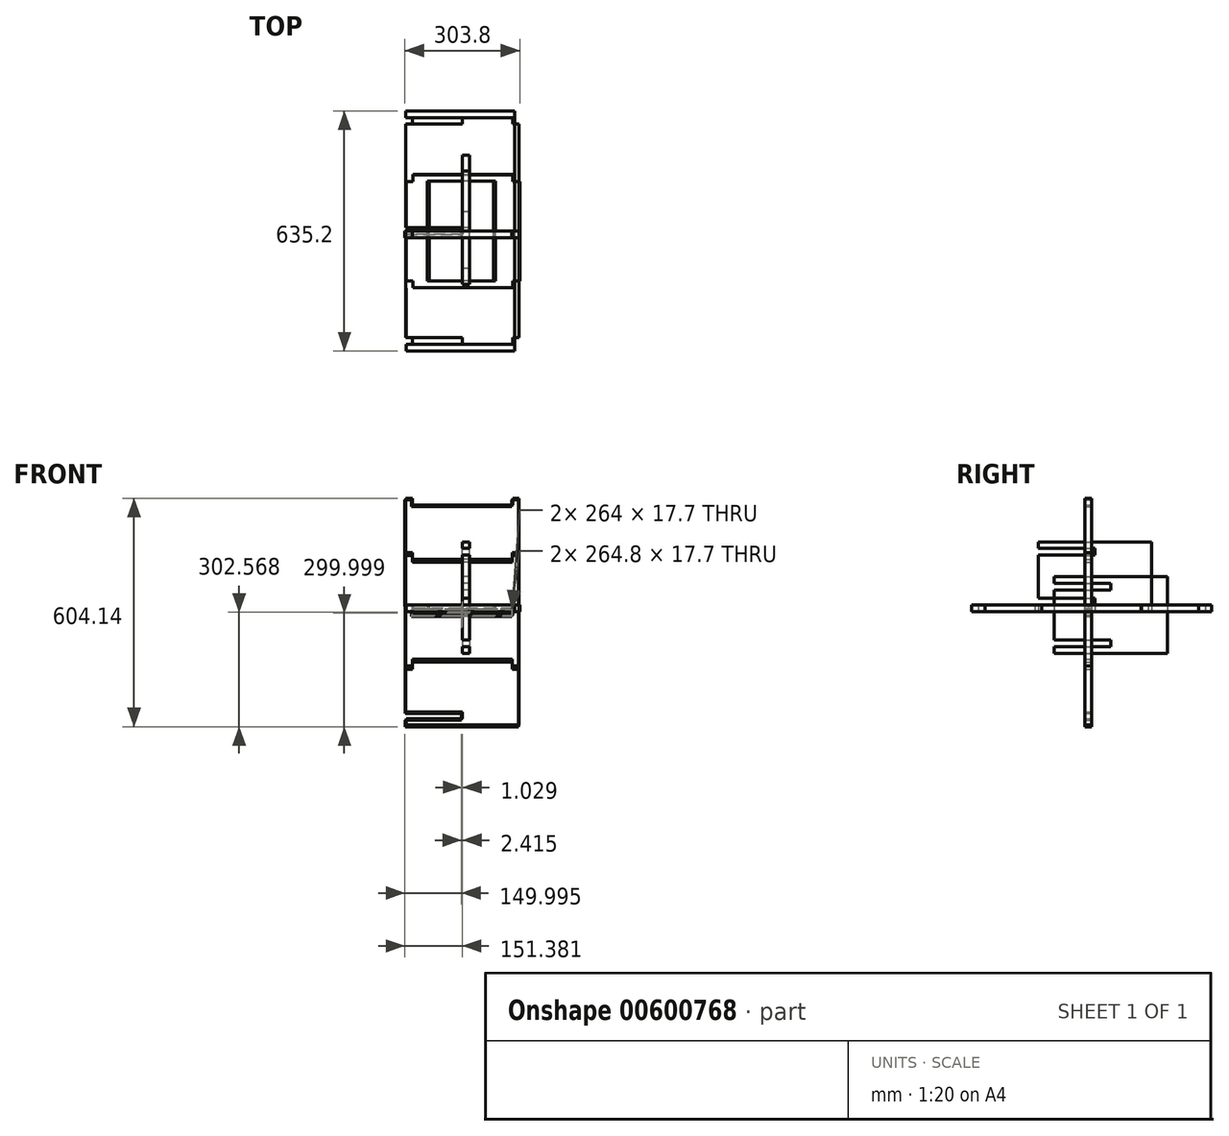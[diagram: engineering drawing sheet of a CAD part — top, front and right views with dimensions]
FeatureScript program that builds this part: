
annotation { "Feature Type Name" : "Feature", "Feature Type Description" : "" }
export const myFeature = defineFeature(function(context is Context, id is Id, definition is map)
    precondition{}
    {
        {
            var Q0;
            Q0=qCreatedBy(makeId("Front.planeOp"),FACE);
            var sketch = newSketch(context, id + "F0", { "sketchPlane" : qUnion([Q0])});
            skLineSegment(sketch, "E0.left", {"start": v(150, -300) * mm, "end": v(150, 300) * mm});
            skLineSegment(sketch, "E1", {"start": v(-150, 300) * mm, "end": v(-132.4, 300) * mm});
            skLineSegment(sketch, "E2", {"start": v(-132.4, 300) * mm, "end": v(-132.4, 282.4) * mm});
            skLineSegment(sketch, "E3", {"start": v(150, 300) * mm, "end": v(132.4, 300) * mm});
            skLineSegment(sketch, "E4", {"start": v(132.4, 300) * mm, "end": v(132.4, 282.4) * mm});
            skLineSegment(sketch, "E5", {"start": v(132.4, 282.4) * mm, "end": v(-132.4, 282.4) * mm});
            skLineSegment(sketch, "E6", {"start": v(150, -300) * mm, "end": v(-149.6, -300) * mm});
            skLineSegment(sketch, "E7", {"start": v(-149.6, -300) * mm, "end": v(-149.6, -282.4) * mm});
            skLineSegment(sketch, "E8", {"start": v(-149.6, -282.4) * mm, "end": v(0, -282.4) * mm});
            skLineSegment(sketch, "E9", {"start": v(0, -282.4) * mm, "end": v(0, -264.8) * mm});
            skLineSegment(sketch, "E10", {"start": v(0, -264.8) * mm, "end": v(-149.73, -264.8) * mm});
            skLineSegment(sketch, "E11", {"start": v(-149.73, -264.8) * mm, "end": v(-150, 300) * mm});
            skLineSegment(sketch, "E12.bottom", {"start": v(132.4, -8.85) * mm, "end": v(-132.4, -8.85) * mm});
            skLineSegment(sketch, "E12.top", {"start": v(132.4, 8.85) * mm, "end": v(-132.4, 8.85) * mm});
            skLineSegment(sketch, "E12.left", {"start": v(132.4, -8.85) * mm, "end": v(132.4, 8.85) * mm});
            skLineSegment(sketch, "E12.right", {"start": v(-132.4, -8.85) * mm, "end": v(-132.4, 8.85) * mm});
            skPoint(sketch, "E12.middle", {"position": v(0, 0) * mm});
            skSolve(sketch);
        }
        {
            var Q0;
            Q0=qCreatedBy(makeId("Front.planeOp"),FACE);
            var sketch = newSketch(context, id + "F1", { "sketchPlane" : qUnion([Q0])});
            skLineSegment(sketch, "E13.left", {"start": v(147.59, -304.14) * mm, "end": v(147.59, 295.86) * mm});
            skLineSegment(sketch, "E14", {"start": v(-152.41, 295.86) * mm, "end": v(-134.81, 295.86) * mm});
            skLineSegment(sketch, "E15", {"start": v(-134.81, 295.86) * mm, "end": v(-134.81, 278.26) * mm});
            skLineSegment(sketch, "E16", {"start": v(147.59, 295.86) * mm, "end": v(129.99, 295.86) * mm});
            skLineSegment(sketch, "E17", {"start": v(129.99, 295.86) * mm, "end": v(129.99, 278.26) * mm});
            skLineSegment(sketch, "E18", {"start": v(129.99, 278.26) * mm, "end": v(-134.81, 278.26) * mm});
            skLineSegment(sketch, "E19", {"start": v(147.59, -304.14) * mm, "end": v(-152.02, -304.14) * mm});
            skLineSegment(sketch, "E20", {"start": v(-152.02, -304.14) * mm, "end": v(-152.02, -286.54) * mm});
            skLineSegment(sketch, "E21", {"start": v(-152.02, -286.54) * mm, "end": v(-2.41, -286.54) * mm});
            skLineSegment(sketch, "E22", {"start": v(-2.41, -286.54) * mm, "end": v(-2.41, -268.94) * mm});
            skLineSegment(sketch, "E23", {"start": v(-2.41, -268.94) * mm, "end": v(-152.15, -268.94) * mm});
            skLineSegment(sketch, "E24", {"start": v(-152.15, -268.94) * mm, "end": v(-152.41, 295.86) * mm});
            skLineSegment(sketch, "E25.bottom", {"start": v(129.99, -13) * mm, "end": v(-134.81, -13) * mm});
            skLineSegment(sketch, "E25.top", {"start": v(129.99, 4.7) * mm, "end": v(-134.81, 4.7) * mm});
            skLineSegment(sketch, "E25.left", {"start": v(129.99, -13) * mm, "end": v(129.99, 4.7) * mm});
            skLineSegment(sketch, "E25.right", {"start": v(-134.81, -13) * mm, "end": v(-134.81, 4.7) * mm});
            skPoint(sketch, "E25.middle", {"position": v(-2.41, -4.14) * mm});
            skSolve(sketch);
        }
        {
            var Q0;
            Q0=qCreatedBy(makeId("Top.planeOp"),FACE);
            var sketch = newSketch(context, id + "F2", { "sketchPlane" : qUnion([Q0])});
            skLineSegment(sketch, "E26.left", {"start": v(149.99, -282.54) * mm, "end": v(149.99, 282.26) * mm});
            skLineSegment(sketch, "E27", {"start": v(-132.41, 299.86) * mm, "end": v(-132.41, 282.26) * mm});
            skLineSegment(sketch, "E28", {"start": v(132.39, 299.86) * mm, "end": v(132.39, 282.26) * mm});
            skLineSegment(sketch, "E29.bottom", {"start": v(0, -9) * mm, "end": v(-132.41, -9) * mm});
            skLineSegment(sketch, "E29.top", {"start": v(0, 8.7) * mm, "end": v(-132.41, 8.7) * mm});
            skPoint(sketch, "E29.middle", {"position": v(-0.01, -0.14) * mm});
            skLineSegment(sketch, "E30", {"start": v(132.39, -300.14) * mm, "end": v(132.39, -282.54) * mm});
            skLineSegment(sketch, "E31", {"start": v(-132.41, -300.14) * mm, "end": v(-132.41, -282.54) * mm});
            skLineSegment(sketch, "E32", {"start": v(-150.01, 282.26) * mm, "end": v(-150.01, 8.7) * mm});
            skLineSegment(sketch, "E33", {"start": v(-132.41, -282.54) * mm, "end": v(-150.01, -282.54) * mm});
            skLineSegment(sketch, "E34", {"start": v(132.39, -282.54) * mm, "end": v(149.99, -282.54) * mm});
            skLineSegment(sketch, "E35", {"start": v(-132.41, -300.14) * mm, "end": v(132.39, -300.14) * mm});
            skLineSegment(sketch, "E36", {"start": v(-132.41, 282.26) * mm, "end": v(-150.01, 282.26) * mm});
            skLineSegment(sketch, "E37", {"start": v(132.39, 282.26) * mm, "end": v(149.99, 282.26) * mm});
            skLineSegment(sketch, "E38", {"start": v(-132.41, 299.86) * mm, "end": v(132.39, 299.86) * mm});
            skLineSegment(sketch, "E39", {"start": v(0, 8.7) * mm, "end": v(0, -9) * mm});
            skLineSegment(sketch, "E40", {"start": v(-132.41, 8.7) * mm, "end": v(-150.01, 8.7) * mm});
            skLineSegment(sketch, "E41", {"start": v(-132.41, -9) * mm, "end": v(-150.01, -9) * mm});
            skLineSegment(sketch, "E42.trimOffspring", {"start": v(-150.01, -9) * mm, "end": v(-150.01, -282.54) * mm});
            skSolve(sketch);
        }
        {
            var Q0;
            Q0=qCreatedBy(makeId("Top.planeOp"),FACE);
            var sketch = newSketch(context, id + "F3", { "sketchPlane" : qUnion([Q0])});
            skLineSegment(sketch, "E43", {"start": v(-149.73, 8.71) * mm, "end": v(0.13, 8.71) * mm});
            skLineSegment(sketch, "E44", {"start": v(-149.73, -9) * mm, "end": v(0, -8.99) * mm});
            skLineSegment(sketch, "E45", {"start": v(0.13, 8.71) * mm, "end": v(0, -8.99) * mm});
            skLineSegment(sketch, "E46", {"start": v(-149.87, 299.86) * mm, "end": v(0, 299.86) * mm});
            skLineSegment(sketch, "E47", {"start": v(-149.48, -300.14) * mm, "end": v(0, -300.14) * mm});
            skLineSegment(sketch, "E48", {"start": v(-149.48, -300.14) * mm, "end": v(-149.48, -317.74) * mm});
            skLineSegment(sketch, "E49", {"start": v(-149.48, -317.74) * mm, "end": v(137.6, -317.74) * mm});
            skLineSegment(sketch, "E50", {"start": v(0, -282.54) * mm, "end": v(0, -300.14) * mm});
            skLineSegment(sketch, "E51", {"start": v(0, -282.54) * mm, "end": v(-149.48, -282.54) * mm});
            skLineSegment(sketch, "E52", {"start": v(-149.73, -9) * mm, "end": v(-149.48, -282.54) * mm});
            skLineSegment(sketch, "E53", {"start": v(137.6, 299.86) * mm, "end": v(137.6, -317.74) * mm});
            skLineSegment(sketch, "E54", {"start": v(-149.86, 282.26) * mm, "end": v(0, 282.33) * mm});
            skLineSegment(sketch, "E55", {"start": v(-149.87, 299.86) * mm, "end": v(-149.87, 317.46) * mm});
            skLineSegment(sketch, "E56", {"start": v(-149.87, 317.46) * mm, "end": v(137.6, 317.46) * mm});
            skLineSegment(sketch, "E57", {"start": v(137.6, 299.86) * mm, "end": v(137.6, 317.46) * mm});
            skLineSegment(sketch, "E58", {"start": v(0, 282.33) * mm, "end": v(0, 299.86) * mm});
            skLineSegment(sketch, "E59", {"start": v(-149.86, 282.26) * mm, "end": v(-149.73, 8.71) * mm});
            skSolve(sketch);
        }
        {
            var Q0;
            Q0=qCreatedBy(makeId("Top.planeOp"),FACE);
            var sketch = newSketch(context, id + "F4", { "sketchPlane" : qUnion([Q0])});
            skLineSegment(sketch, "E60.bottom", {"start": v(133.13, -150.22) * mm, "end": v(-131.67, -150.22) * mm});
            skPoint(sketch, "E60.middle", {"position": v(0.33, -0.22) * mm});
            skLineSegment(sketch, "E61.left", {"start": v(133.13, 130.98) * mm, "end": v(133.13, 148.98) * mm});
            skLineSegment(sketch, "E61.right", {"start": v(-131.67, 130.98) * mm, "end": v(-131.67, 148.98) * mm});
            skLineSegment(sketch, "E62.left", {"start": v(133.13, -132.22) * mm, "end": v(133.13, -150.22) * mm});
            skLineSegment(sketch, "E62.right", {"start": v(-131.67, -132.22) * mm, "end": v(-131.67, -150.22) * mm});
            skLineSegment(sketch, "E63", {"start": v(-131.67, 148.98) * mm, "end": v(133.13, 148.98) * mm});
            skLineSegment(sketch, "E64", {"start": v(-131.67, 130.98) * mm, "end": v(-149.67, 130.98) * mm});
            skLineSegment(sketch, "E65", {"start": v(133.13, 130.98) * mm, "end": v(151.13, 130.98) * mm});
            skLineSegment(sketch, "E66", {"start": v(-131.67, -132.22) * mm, "end": v(-149.67, -132.22) * mm});
            skLineSegment(sketch, "E67", {"start": v(133.13, -132.22) * mm, "end": v(151.13, -132.22) * mm});
            skLineSegment(sketch, "E68", {"start": v(0.33, 8.38) * mm, "end": v(0.33, -9.22) * mm});
            skLineSegment(sketch, "E69.trimOffspring", {"start": v(-149.67, 8.38) * mm, "end": v(-149.67, 130.98) * mm});
            skLineSegment(sketch, "E70", {"start": v(-149.67, -132.22) * mm, "end": v(-149.67, -9.22) * mm});
            skLineSegment(sketch, "E71", {"start": v(151.13, -132.22) * mm, "end": v(151.13, 130.98) * mm});
            skLineSegment(sketch, "E72", {"start": v(-149.67, -9.22) * mm, "end": v(0.33, -9.22) * mm});
            skLineSegment(sketch, "E73", {"start": v(-149.67, 8.38) * mm, "end": v(0.33, 8.38) * mm});
            skSolve(sketch);
        }
        {
            var Q0;
            Q0=qCreatedBy(makeId("Top.planeOp"),FACE);
            var sketch = newSketch(context, id + "F5", { "sketchPlane" : qUnion([Q0])});
            skLineSegment(sketch, "E74.bottom", {"start": v(133.4, -150.43) * mm, "end": v(-131.4, -150.43) * mm});
            skPoint(sketch, "E74.middle", {"position": v(0.6, -0.43) * mm});
            skLineSegment(sketch, "E75.left", {"start": v(133.4, 130.77) * mm, "end": v(133.4, 148.77) * mm});
            skLineSegment(sketch, "E75.right", {"start": v(-131.4, 130.77) * mm, "end": v(-131.4, 148.77) * mm});
            skLineSegment(sketch, "E76.left", {"start": v(133.4, -132.43) * mm, "end": v(133.4, -150.43) * mm});
            skLineSegment(sketch, "E76.right", {"start": v(-131.4, -132.43) * mm, "end": v(-131.4, -150.43) * mm});
            skLineSegment(sketch, "E77", {"start": v(-131.4, 148.77) * mm, "end": v(133.4, 148.77) * mm});
            skLineSegment(sketch, "E78", {"start": v(-131.4, 130.77) * mm, "end": v(-149.4, 130.77) * mm});
            skLineSegment(sketch, "E79", {"start": v(133.4, 130.77) * mm, "end": v(151.4, 130.77) * mm});
            skLineSegment(sketch, "E80", {"start": v(-131.4, -132.43) * mm, "end": v(-149.4, -132.43) * mm});
            skLineSegment(sketch, "E81", {"start": v(133.4, -132.43) * mm, "end": v(151.4, -132.43) * mm});
            skLineSegment(sketch, "E82", {"start": v(0.6, 8.17) * mm, "end": v(0.6, -9.43) * mm});
            skLineSegment(sketch, "E83.trimOffspring", {"start": v(-149.4, 8.17) * mm, "end": v(-149.4, 130.77) * mm});
            skLineSegment(sketch, "E84", {"start": v(-149.4, -132.43) * mm, "end": v(-149.4, -9.43) * mm});
            skLineSegment(sketch, "E85", {"start": v(151.4, -132.43) * mm, "end": v(151.4, 130.77) * mm});
            skLineSegment(sketch, "E86", {"start": v(-149.4, -9.43) * mm, "end": v(0.6, -9.43) * mm});
            skLineSegment(sketch, "E87", {"start": v(-149.4, 8.17) * mm, "end": v(0.6, 8.17) * mm});
            skSolve(sketch);
        }
        {
            var Q0;
            Q0=qCreatedBy(makeId("Front.planeOp"),FACE);
            var sketch = newSketch(context, id + "F6", { "sketchPlane" : qUnion([Q0])});
            skLineSegment(sketch, "E88.bottom", {"start": v(148.97, -151.57) * mm, "end": v(130.97, -151.57) * mm});
            skLineSegment(sketch, "E88.top", {"start": v(148.97, 148.43) * mm, "end": v(130.97, 148.43) * mm});
            skLineSegment(sketch, "E88.left", {"start": v(148.97, -151.57) * mm, "end": v(148.97, 148.43) * mm});
            skLineSegment(sketch, "E89.left", {"start": v(130.97, -10.42) * mm, "end": v(130.97, 7.28) * mm});
            skLineSegment(sketch, "E90.bottom", {"start": v(130.97, 130.58) * mm, "end": v(-133.03, 130.58) * mm});
            skLineSegment(sketch, "E90.left", {"start": v(130.97, 130.58) * mm, "end": v(130.97, 148.43) * mm});
            skLineSegment(sketch, "E90.right", {"start": v(-133.03, 130.58) * mm, "end": v(-133.03, 148.43) * mm});
            skLineSegment(sketch, "E91.trimOffspring", {"start": v(-133.03, 148.43) * mm, "end": v(-151.03, 148.43) * mm});
            skLineSegment(sketch, "E92", {"start": v(-1.03, -133.42) * mm, "end": v(-133.03, -133.42) * mm});
            skLineSegment(sketch, "E93.trimOffspring", {"start": v(-133.03, -133.42) * mm, "end": v(-133.03, -151.57) * mm});
            skLineSegment(sketch, "E94", {"start": v(-1.03, -133.42) * mm, "end": v(130.97, -133.42) * mm});
            skLineSegment(sketch, "E95.trimOffspring", {"start": v(130.97, -133.42) * mm, "end": v(130.97, -151.57) * mm});
            skLineSegment(sketch, "E96.trimOffspring", {"start": v(-133.03, -151.57) * mm, "end": v(-151.03, -151.57) * mm});
            skLineSegment(sketch, "E97", {"start": v(-151.03, 148.43) * mm, "end": v(-151.03, -151.57) * mm});
            skLineSegment(sketch, "E98", {"start": v(130.97, 7.28) * mm, "end": v(-133.03, 7.28) * mm});
            skLineSegment(sketch, "E99", {"start": v(-133.03, 7.28) * mm, "end": v(-133.03, -10.42) * mm});
            skLineSegment(sketch, "E100", {"start": v(-133.03, -10.42) * mm, "end": v(130.97, -10.42) * mm});
            skSolve(sketch);
        }
        {
            var Q0;
            Q0=qCreatedBy(makeId("Front.planeOp"),FACE);
            var sketch = newSketch(context, id + "F7", { "sketchPlane" : qUnion([Q0])});
            skLineSegment(sketch, "E101.bottom", {"start": v(150, -143.75) * mm, "end": v(132, -143.75) * mm});
            skLineSegment(sketch, "E101.top", {"start": v(150, 156.25) * mm, "end": v(132, 156.25) * mm});
            skLineSegment(sketch, "E101.left", {"start": v(150, -143.75) * mm, "end": v(150, 156.25) * mm});
            skPoint(sketch, "E101.middle", {"position": v(0, 6.25) * mm});
            skLineSegment(sketch, "E102.bottom", {"start": v(132, -2.6) * mm, "end": v(-132, -2.6) * mm});
            skLineSegment(sketch, "E102.top", {"start": v(132, 15.1) * mm, "end": v(-132, 15.1) * mm});
            skLineSegment(sketch, "E102.left", {"start": v(132, -2.6) * mm, "end": v(132, 15.1) * mm});
            skLineSegment(sketch, "E102.right", {"start": v(-132, -2.6) * mm, "end": v(-132, 15.1) * mm});
            skLineSegment(sketch, "E103.bottom", {"start": v(132, 138.4) * mm, "end": v(-132, 138.4) * mm});
            skLineSegment(sketch, "E103.left", {"start": v(132, 138.4) * mm, "end": v(132, 156.25) * mm});
            skLineSegment(sketch, "E103.right", {"start": v(-132, 138.4) * mm, "end": v(-132, 156.25) * mm});
            skLineSegment(sketch, "E104.trimOffspring", {"start": v(-132, 156.25) * mm, "end": v(-150, 156.25) * mm});
            skLineSegment(sketch, "E105", {"start": v(0, -125.6) * mm, "end": v(-132, -125.6) * mm});
            skLineSegment(sketch, "E106", {"start": v(-132, 15.1) * mm, "end": v(-132, -2.6) * mm});
            skLineSegment(sketch, "E107.trimOffspring", {"start": v(-132, -125.6) * mm, "end": v(-132, -143.75) * mm});
            skLineSegment(sketch, "E108", {"start": v(0, -125.6) * mm, "end": v(132, -125.6) * mm});
            skLineSegment(sketch, "E109", {"start": v(132, 15.1) * mm, "end": v(132, -2.6) * mm});
            skLineSegment(sketch, "E110.trimOffspring", {"start": v(132, -125.6) * mm, "end": v(132, -143.75) * mm});
            skLineSegment(sketch, "E111.trimOffspring", {"start": v(-132, -143.75) * mm, "end": v(-150, -143.75) * mm});
            skLineSegment(sketch, "E112", {"start": v(-150, 156.25) * mm, "end": v(-150, -143.75) * mm});
            skSolve(sketch);
        }
        {
            var Q0;
            Q0=qCreatedBy(makeId("Top.planeOp"),FACE);
            var sketch = newSketch(context, id + "F8", { "sketchPlane" : qUnion([Q0])});
            skLineSegment(sketch, "E113.bottom", {"start": v(87.5, -132.2) * mm, "end": v(-87.5, -132.2) * mm});
            skLineSegment(sketch, "E113.top", {"start": v(87.5, 132.2) * mm, "end": v(-87.5, 132.2) * mm});
            skLineSegment(sketch, "E113.left", {"start": v(87.5, -132.2) * mm, "end": v(87.5, 132.2) * mm});
            skLineSegment(sketch, "E113.right", {"start": v(-87.5, -132.2) * mm, "end": v(-87.5, 132.2) * mm});
            skPoint(sketch, "E113.middle", {"position": v(0, 0) * mm});
            skSolve(sketch);
        }
        {
            var Q0;
            Q0=qCreatedBy(makeId("Top.planeOp"),FACE);
            var sketch = newSketch(context, id + "F9", { "sketchPlane" : qUnion([Q0])});
            skLineSegment(sketch, "E114.bottom", {"start": v(82.4, -132.4) * mm, "end": v(-92.6, -132.4) * mm});
            skLineSegment(sketch, "E114.top", {"start": v(82.4, 132) * mm, "end": v(-92.6, 132) * mm});
            skLineSegment(sketch, "E114.left", {"start": v(82.4, -132.4) * mm, "end": v(82.4, 132) * mm});
            skLineSegment(sketch, "E114.right", {"start": v(-92.6, -132.4) * mm, "end": v(-92.6, 132) * mm});
            skPoint(sketch, "E114.middle", {"position": v(-5.1, -0.2) * mm});
            skSolve(sketch);
        }
        {
            var Q0;
            Q0=qCreatedBy(makeId("Right.planeOp"),FACE);
            var sketch = newSketch(context, id + "F10", { "sketchPlane" : qUnion([Q0])});
            skLineSegment(sketch, "E115.bottom", {"start": v(-141.34, 17.6) * mm, "end": v(8.66, 17.6) * mm});
            skLineSegment(sketch, "E116", {"start": v(-141.34, 167.4) * mm, "end": v(-141.34, 185) * mm});
            skLineSegment(sketch, "E117", {"start": v(-141.34, 185) * mm, "end": v(158.66, 185) * mm});
            skLineSegment(sketch, "E118", {"start": v(-141.34, 167.4) * mm, "end": v(8.66, 167.4) * mm});
            skLineSegment(sketch, "E119", {"start": v(8.66, 149.8) * mm, "end": v(8.66, 167.4) * mm});
            skLineSegment(sketch, "E120", {"start": v(-141.34, 17.6) * mm, "end": v(-141.34, 0) * mm});
            skLineSegment(sketch, "E121", {"start": v(8.66, 35.2) * mm, "end": v(8.66, 17.6) * mm});
            skLineSegment(sketch, "E122", {"start": v(-141.34, 0) * mm, "end": v(158.66, 0) * mm});
            skLineSegment(sketch, "E123", {"start": v(-141.34, 149.8) * mm, "end": v(8.66, 149.8) * mm});
            skLineSegment(sketch, "E124", {"start": v(-141.34, 35.27) * mm, "end": v(8.66, 35.2) * mm});
            skLineSegment(sketch, "E125", {"start": v(158.66, 185) * mm, "end": v(158.66, -0.2) * mm});
            skLineSegment(sketch, "E126", {"start": v(-141.34, 149.8) * mm, "end": v(-141.34, 35.27) * mm});
            skSolve(sketch);
        }
        {
            var Q0;
            Q0=qCreatedBy(makeId("Right.planeOp"),FACE);
            var sketch = newSketch(context, id + "F11", { "sketchPlane" : qUnion([Q0])});
            skLineSegment(sketch, "E127.bottom", {"start": v(-100, -92.7) * mm, "end": v(50, -92.7) * mm});
            skLineSegment(sketch, "E128", {"start": v(-100, 74.9) * mm, "end": v(-100, 92.5) * mm});
            skLineSegment(sketch, "E129", {"start": v(-100, 92.5) * mm, "end": v(200, 92.5) * mm});
            skLineSegment(sketch, "E130", {"start": v(-100, 74.9) * mm, "end": v(50, 74.9) * mm});
            skLineSegment(sketch, "E131", {"start": v(50, 57.3) * mm, "end": v(50, 74.9) * mm});
            skLineSegment(sketch, "E132", {"start": v(-100, -92.7) * mm, "end": v(-100, -110.3) * mm});
            skLineSegment(sketch, "E133", {"start": v(50, -75.1) * mm, "end": v(50, -92.7) * mm});
            skLineSegment(sketch, "E134", {"start": v(-100, -110.3) * mm, "end": v(200, -110.3) * mm});
            skLineSegment(sketch, "E135", {"start": v(-100, 57.3) * mm, "end": v(50, 57.3) * mm});
            skLineSegment(sketch, "E136", {"start": v(-100, -75.02) * mm, "end": v(50, -75.1) * mm});
            skLineSegment(sketch, "E137", {"start": v(200, 92.5) * mm, "end": v(200, -110.3) * mm});
            skLineSegment(sketch, "E138", {"start": v(-100, 57.3) * mm, "end": v(-100, -75.02) * mm});
            skSolve(sketch);
        }
        {
            var Q0;
            Q0 = qSketchRegion(id + "F0", true);
            extrude(context, id + "F12", {"entities" : qUnion([Q0]), "depth" : 18 * mm, "offsetDistance" : 25 * mm});
        }
        {
            var Q0;
            Q0 = qSketchRegion(id + "F1", true);
            extrude(context, id + "F13", {"entities" : qUnion([Q0]), "depth" : 18 * mm, "offsetDistance" : 25 * mm});
        }
        {
            var Q0;
            Q0 = qSketchRegion(id + "F2", true);
            extrude(context, id + "F14", {"entities" : qUnion([Q0]), "depth" : 18 * mm, "offsetDistance" : 25 * mm});
        }
        {
            var Q0;
            Q0 = qSketchRegion(id + "F3", true);
            extrude(context, id + "F15", {"entities" : qUnion([Q0]), "depth" : 18 * mm, "offsetDistance" : 25 * mm});
        }
        {
            var Q0;
            Q0 = qSketchRegion(id + "F4", true);
            extrude(context, id + "F16", {"entities" : qUnion([Q0]), "depth" : 18 * mm, "offsetDistance" : 25 * mm});
        }
        {
            var Q0;
            Q0 = qSketchRegion(id + "F5", true);
            extrude(context, id + "F17", {"entities" : qUnion([Q0]), "depth" : 18 * mm, "offsetDistance" : 25 * mm});
        }
        {
            var Q0;
            Q0 = qSketchRegion(id + "F6", true);
            extrude(context, id + "F18", {"entities" : qUnion([Q0]), "depth" : 18 * mm, "offsetDistance" : 25 * mm});
        }
        {
            var Q0;
            Q0 = qSketchRegion(id + "F7", true);
            extrude(context, id + "F19", {"entities" : qUnion([Q0]), "depth" : 18 * mm, "offsetDistance" : 25 * mm});
        }
        {
            var Q0;
            Q0 = qSketchRegion(id + "F8", true);
            extrude(context, id + "F20", {"entities" : qUnion([Q0]), "depth" : 18 * mm, "offsetDistance" : 25 * mm});
        }
        {
            var Q0;
            Q0 = qSketchRegion(id + "F9", true);
            extrude(context, id + "F21", {"entities" : qUnion([Q0]), "depth" : 18 * mm, "offsetDistance" : 25 * mm});
        }
        {
            var Q0;
            Q0 = qSketchRegion(id + "F10", true);
            extrude(context, id + "F22", {"entities" : qUnion([Q0]), "depth" : 18 * mm, "offsetDistance" : 25 * mm});
        }
        {
            var Q0;
            Q0 = qSketchRegion(id + "F11", true);
            extrude(context, id + "F23", {"entities" : qUnion([Q0]), "depth" : 18 * mm, "offsetDistance" : 25 * mm});
        }
    });
